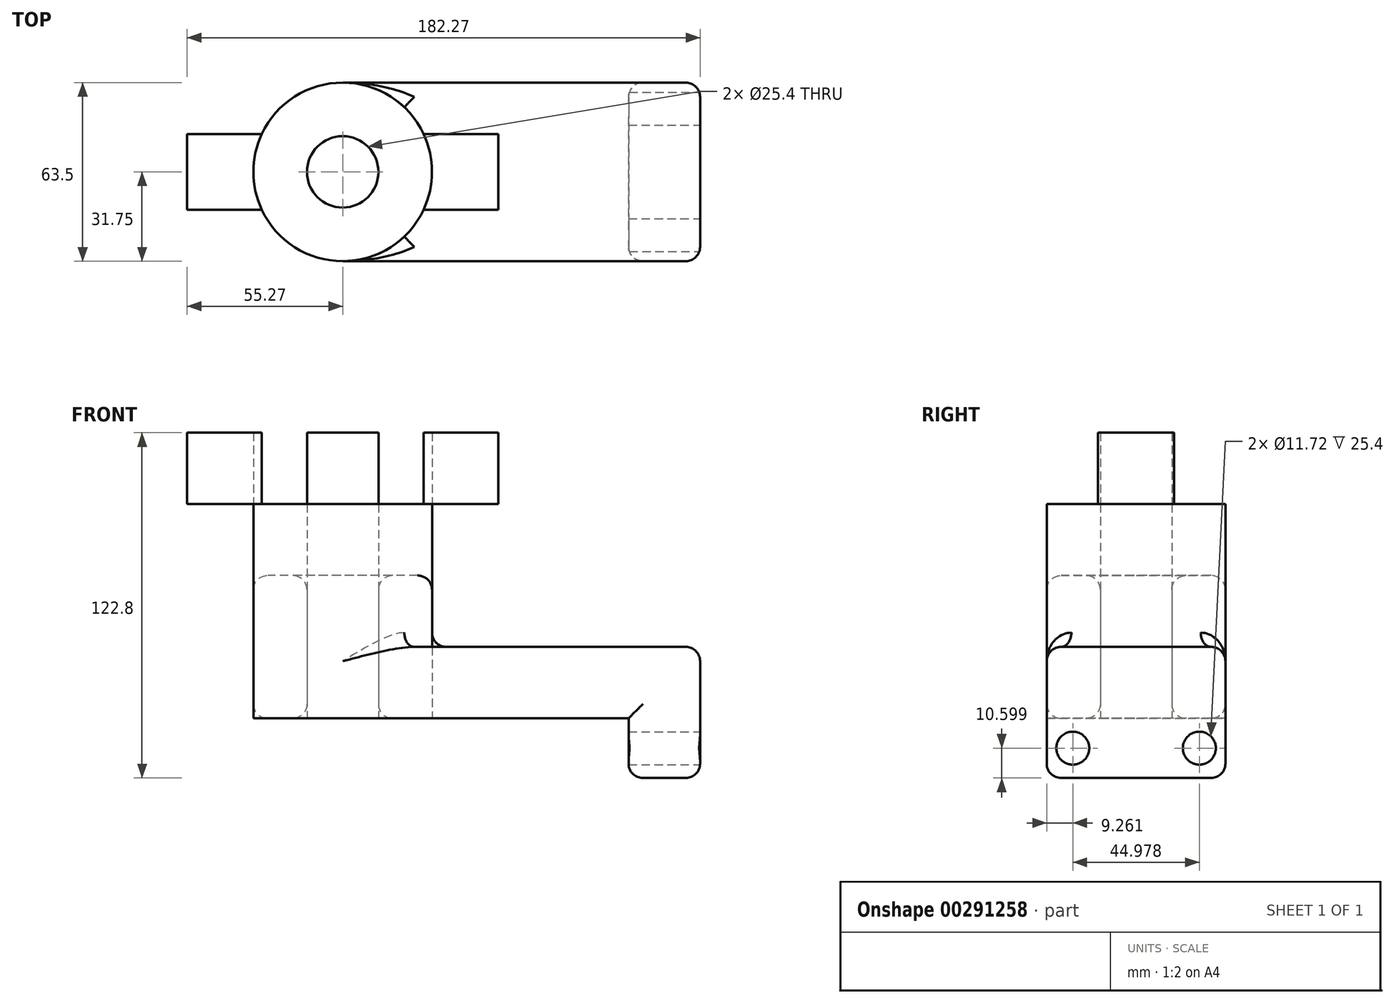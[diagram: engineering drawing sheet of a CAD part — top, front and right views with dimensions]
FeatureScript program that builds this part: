
annotation { "Feature Type Name" : "Feature", "Feature Type Description" : "" }
export const myFeature = defineFeature(function(context is Context, id is Id, definition is map)
    precondition{}
    {
        {
            var Q0;
            Q0=qCreatedBy(makeId("Top.planeOp"),FACE);
            var sketch = newSketch(context, id + "F0", { "sketchPlane" : qUnion([Q0])});
            skLineSegment(sketch, "E0.bottom", {"start": v(0, 0) * mm, "end": v(127, 0) * mm});
            skLineSegment(sketch, "E0.top", {"start": v(0, -63.5) * mm, "end": v(127, -63.5) * mm});
            skLineSegment(sketch, "E0.left", {"start": v(0, 0) * mm, "end": v(0, -63.5) * mm});
            skLineSegment(sketch, "E0.right", {"start": v(127, 0) * mm, "end": v(127, -63.5) * mm});
            skCircle(sketch, "E1", {"center": v(0, -31.75) * mm, "radius": 31.75 * mm});
            skCircle(sketch, "E2", {"center": v(0, -31.75) * mm, "radius": 12.7 * mm});
            skSolve(sketch);
        }
        {
            var Q0;
            {var subQ1=sQuery(id+"F0.wireOp",EDGE,"E0.left");var subQ3=sQuery(id+"F0.wireOp",EDGE,"E2");var subQ4=makeQuery(id+"F0.imprint","INTERSECT",VERTEX,{"disambiguationData":[OD(0.0)],"derivedFrom":[subQ1,subQ3]});Q0=makeQuery(id+"F0.imprint","IMPRINT",FACE,{"disambiguationData":[TD([[makeQuery(id+"F0.imprint","IMPRINT",EDGE,{"disambiguationData":[TD([[subQ4,-1.0]])],"derivedFrom":subQ3}),-1.0]])]});}
            var Q1;
            {var subQ1=sQuery(id+"F0.wireOp",EDGE,"E0.left");var subQ3=sQuery(id+"F0.wireOp",EDGE,"E2");var subQ4=makeQuery(id+"F0.imprint","INTERSECT",VERTEX,{"disambiguationData":[OD(0.0)],"derivedFrom":[subQ1,subQ3]});Q1=makeQuery(id+"F0.imprint","IMPRINT",FACE,{"disambiguationData":[TD([[makeQuery(id+"F0.imprint","IMPRINT",EDGE,{"disambiguationData":[TD([[subQ4,1.0]])],"derivedFrom":subQ3}),-1.0]])]});}
            var Q2;
            {var subQ0=sQuery(id+"F0.wireOp",EDGE,"E0.bottom");Q2=makeQuery(id+"F0.imprint","IMPRINT",FACE,{"disambiguationData":[TD([[makeQuery(id+"F0.imprint","IMPRINT",EDGE,{"derivedFrom":subQ0}),-1.0]])]});}
            extrude(context, id + "F1", {"entities" : qUnion([Q0, Q1, Q2]), "depth" : 25.4 * mm});
        }
        {
            var Q0;
            {var subQ1=sQuery(id+"F0.wireOp",EDGE,"E0.left");var subQ3=sQuery(id+"F0.wireOp",EDGE,"E2");var subQ4=makeQuery(id+"F0.imprint","INTERSECT",VERTEX,{"disambiguationData":[OD(0.0)],"derivedFrom":[subQ1,subQ3]});Q0=makeQuery(id+"F0.imprint","IMPRINT",FACE,{"disambiguationData":[TD([[makeQuery(id+"F0.imprint","IMPRINT",EDGE,{"disambiguationData":[TD([[subQ4,-1.0]])],"derivedFrom":subQ3}),-1.0]])]});}
            var Q1;
            {var subQ1=sQuery(id+"F0.wireOp",EDGE,"E0.left");var subQ3=sQuery(id+"F0.wireOp",EDGE,"E2");var subQ4=makeQuery(id+"F0.imprint","INTERSECT",VERTEX,{"disambiguationData":[OD(0.0)],"derivedFrom":[subQ1,subQ3]});Q1=makeQuery(id+"F0.imprint","IMPRINT",FACE,{"disambiguationData":[TD([[makeQuery(id+"F0.imprint","IMPRINT",EDGE,{"disambiguationData":[TD([[subQ4,1.0]])],"derivedFrom":subQ3}),-1.0]])]});}
            extrude(context, id + "F2", {"entities" : qUnion([Q0, Q1]), "operationType" : NewBodyOperationType.ADD, "depth" : 50.8 * mm});
        }
        {
            var Q0;
            Q0=makeQuery(id+"F1.opExtrude","SWEPT_FACE",FACE,{"disambiguationData":[OSD([sQuery(id+"F0.wireOp",EDGE,"E0.right")])]});
            var sketch = newSketch(context, id + "F3", { "sketchPlane" : qUnion([Q0])});
            skLineSegment(sketch, "E3.bottom", {"start": v(-63.5, 0) * mm, "end": v(0, 0) * mm});
            skLineSegment(sketch, "E3.top", {"start": v(-63.5, -21.2) * mm, "end": v(0, -21.2) * mm});
            skLineSegment(sketch, "E3.left", {"start": v(-63.5, 0) * mm, "end": v(-63.5, -21.2) * mm});
            skLineSegment(sketch, "E3.right", {"start": v(0, 0) * mm, "end": v(0, -21.2) * mm});
            skLineSegment(sketch, "E4", {"start": v(-31.75, 0) * mm, "end": v(-31.75, -21.2) * mm, "construction": true});
            skCircle(sketch, "E5", {"center": v(-54.24, -10.6) * mm, "radius": 5.86 * mm});
            skPoint(sketch, "E5.centerSnap0", {"position": v(-63.5, -10.6) * mm});
            skCircle(sketch, "E6.MirrorC", {"center": v(-9.26, -10.6) * mm, "radius": 5.86 * mm});
            skSolve(sketch);
        }
        {
            var Q0;
            Q0=makeQuery(id+"F3.imprint","IMPRINT",FACE,{"disambiguationData":[TD([[makeQuery(id+"F3.imprint","IMPRINT",EDGE,{"derivedFrom":sQuery(id+"F3.wireOp",EDGE,"E3.bottom")}),1.0]])]});
            extrude(context, id + "F4", {"entities" : qUnion([Q0]), "operationType" : NewBodyOperationType.ADD, "oppositeDirection" : true, "depth" : 25.4 * mm});
        }
        {
            var Q0;
            {var subQ0=sQuery(id+"F0.wireOp",EDGE,"E2");Q0=makeQuery(id+"F2.boolean.opBoolean","MERGE",FACE,{"derivedFrom":[makeQuery(id+"F1.opExtrude","SWEPT_FACE",FACE,{"disambiguationData":[OSD([subQ0])]}),makeQuery(id+"F2.opExtrude","SWEPT_FACE",FACE,{"disambiguationData":[OSD([subQ0])]})]});}
            var Q1;
            Q1=makeQuery(id+"F1.opExtrude","CAP_FACE",FACE,{"disambiguationData":[OSD([sQuery(id+"F0.wireOp",EDGE,"E0.bottom"),sQuery(id+"F0.wireOp",EDGE,"E0.top"),sQuery(id+"F0.wireOp",EDGE,"E0.right"),sQuery(id+"F0.wireOp",EDGE,"E1"),sQuery(id+"F0.wireOp",EDGE,"E2")])],"isStart":false});
            var Q2;
            Q2=makeQuery(id+"F2.opExtrude","CAP_EDGE",EDGE,{"disambiguationData":[OSD([sQuery(id+"F0.wireOp",EDGE,"E1")])],"isStart":false});
            var Q3;
            Q3=makeQuery(id+"F4.opExtrude","CAP_EDGE",EDGE,{"disambiguationData":[OSD([sQuery(id+"F3.wireOp",EDGE,"E3.top")])],"isStart":true});
            var Q4;
            Q4=makeQuery(id+"F4.boolean.opBoolean","MERGE",EDGE,{"derivedFrom":[makeQuery(id+"F1.opExtrude","SWEPT_EDGE",EDGE,{"disambiguationData":[OSD([sQuery(id+"F0.wireOp",EDGE,"E0.bottom"),sQuery(id+"F0.wireOp",EDGE,"E0.right")])]}),makeQuery(id+"F4.opExtrude","CAP_EDGE",EDGE,{"disambiguationData":[OSD([sQuery(id+"F3.wireOp",EDGE,"E3.right")])],"isStart":true})]});
            var Q5;
            Q5=makeQuery(id+"F4.boolean.opBoolean","MERGE",EDGE,{"derivedFrom":[makeQuery(id+"F1.opExtrude","SWEPT_EDGE",EDGE,{"disambiguationData":[OSD([sQuery(id+"F0.wireOp",EDGE,"E0.top"),sQuery(id+"F0.wireOp",EDGE,"E0.right")])]}),makeQuery(id+"F4.opExtrude","CAP_EDGE",EDGE,{"disambiguationData":[OSD([sQuery(id+"F3.wireOp",EDGE,"E3.left")])],"isStart":true})]});
            var Q6;
            Q6=makeQuery(id+"F1.opExtrude","CAP_EDGE",EDGE,{"disambiguationData":[OSD([sQuery(id+"F0.wireOp",EDGE,"E0.bottom")])],"isStart":true});
            var Q7;
            Q7=makeQuery(id+"F4.opExtrude","CAP_EDGE",EDGE,{"disambiguationData":[OSD([sQuery(id+"F3.wireOp",EDGE,"E3.right")])],"isStart":false});
            var Q8;
            Q8=makeQuery(id+"F4.opExtrude","SWEPT_EDGE",EDGE,{"disambiguationData":[OSD([sQuery(id+"F3.wireOp",EDGE,"E3.top"),sQuery(id+"F3.wireOp",EDGE,"E3.right")])]});
            var Q9;
            Q9=makeQuery(id+"F4.boolean.opBoolean","MERGE",FACE,{"derivedFrom":[makeQuery(id+"F1.opExtrude","SWEPT_FACE",FACE,{"disambiguationData":[OSD([sQuery(id+"F0.wireOp",EDGE,"E0.top")])]}),makeQuery(id+"F4.opExtrude","SWEPT_FACE",FACE,{"disambiguationData":[OSD([sQuery(id+"F3.wireOp",EDGE,"E3.left")])]})]});
            fillet(context, id + "F5", {"entities" : qUnion([Q0, Q1, Q2, Q3, Q4, Q5, Q6, Q7, Q8, Q9]), "radius" : 5.08 * mm, "tangentPropagation" : true, "allowEdgeOverflow" : false});
        }
        {
            var Q0;
            Q0=makeQuery(id+"F4.opExtrude","CAP_EDGE",EDGE,{"disambiguationData":[OSD([sQuery(id+"F3.wireOp",EDGE,"E3.top")])],"isStart":false});
            fillet(context, id + "F6", {"entities" : qUnion([Q0]), "radius" : 5.08 * mm, "tangentPropagation" : true, "allowEdgeOverflow" : false});
        }
        {
            var Q0;
            {var subQ0=sQuery(id+"F0.wireOp",EDGE,"E2");var subQ1=sQuery(id+"F0.wireOp",EDGE,"E0.left");var subQ2=makeQuery(id+"F0.imprint","INTERSECT",VERTEX,{"disambiguationData":[OD(0.0)],"derivedFrom":[subQ1,subQ0]});Q0=makeQuery(id+"F0.imprint","IMPRINT",FACE,{"disambiguationData":[TD([[makeQuery(id+"F0.imprint","IMPRINT",EDGE,{"disambiguationData":[TD([[subQ2,-1.0]])],"derivedFrom":subQ1}),1.0]])]});}
            var Q1;
            {var subQ0=sQuery(id+"F0.wireOp",EDGE,"E2");var subQ1=sQuery(id+"F0.wireOp",EDGE,"E0.left");var subQ2=makeQuery(id+"F0.imprint","INTERSECT",VERTEX,{"disambiguationData":[OD(0.0)],"derivedFrom":[subQ1,subQ0]});Q1=makeQuery(id+"F0.imprint","IMPRINT",FACE,{"disambiguationData":[TD([[makeQuery(id+"F0.imprint","IMPRINT",EDGE,{"disambiguationData":[TD([[subQ2,-1.0]])],"derivedFrom":subQ1}),-1.0]])]});}
            extrude(context, id + "F7", {"entities" : qUnion([Q0, Q1]), "depth" : 76.2 * mm});
        }
        {
            var Q0;
            Q0=makeQuery(id+"F7.opExtrude","CAP_FACE",FACE,{"disambiguationData":[OSD([sQuery(id+"F0.wireOp",EDGE,"E2")])],"isStart":false});
            var sketch = newSketch(context, id + "F8", { "sketchPlane" : qUnion([Q0])});
            skLineSegment(sketch, "E7.bottom", {"start": v(-55.27, -18.27) * mm, "end": v(55.27, -18.27) * mm});
            skLineSegment(sketch, "E7.top", {"start": v(-55.27, -45.23) * mm, "end": v(55.27, -45.23) * mm});
            skLineSegment(sketch, "E7.left", {"start": v(-55.27, -18.27) * mm, "end": v(-55.27, -45.23) * mm});
            skLineSegment(sketch, "E7.right", {"start": v(55.27, -18.27) * mm, "end": v(55.27, -45.23) * mm});
            skPoint(sketch, "E7.middle", {"position": v(0, -31.75) * mm});
            skSolve(sketch);
        }
        {
            var Q0;
            Q0=makeQuery(id+"F8.imprint","IMPRINT",FACE,{"disambiguationData":[TD([[makeQuery(id+"F8.imprint","IMPRINT",EDGE,{"derivedFrom":makeQuery(id+"F7.opExtrude","CAP_EDGE",EDGE,{"disambiguationData":[OSD([sQuery(id+"F0.wireOp",EDGE,"E2")])],"isStart":false})}),1.0]])]});
            var Q1;
            Q1=makeQuery(id+"F8.imprint","IMPRINT",FACE,{"disambiguationData":[TD([[makeQuery(id+"F8.imprint","IMPRINT",EDGE,{"derivedFrom":sQuery(id+"F8.wireOp",EDGE,"E7.bottom")}),-1.0]])]});
            extrude(context, id + "F9", {"entities" : qUnion([Q0, Q1]), "operationType" : NewBodyOperationType.ADD, "depth" : 25.4 * mm});
        }
    });
